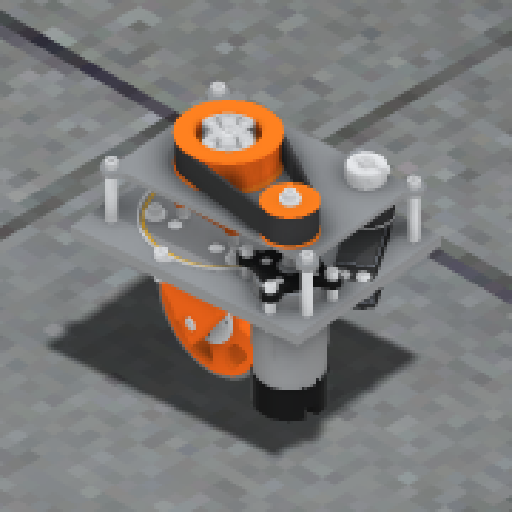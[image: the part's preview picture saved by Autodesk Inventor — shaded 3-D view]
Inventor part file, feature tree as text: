
AUTODESK INVENTOR PART (.ipt)
format: ipt  version: 2024.2 (Build 282272000, 272)  size: 62,777,856 bytes
history: native  units: in
note: dims shown in document units (in); Inventor stores cm internally (conversion verified against a paired STEP export)
features: other x3, plane x1
ambient origin geometry x8: Origin, YZ Plane, XZ Plane, XY Plane, X Axis, Y Axis, Z Axis, Center Point
bodies: Solid1 (feature_tree)
feature tree (4):
  other  "Pod_pre_mirror.ipt"
  other  "Solid1::Pod_pre_mirror.ipt"
  other  "TaggingFeature1"
  plane  "Work Plane2_1"
